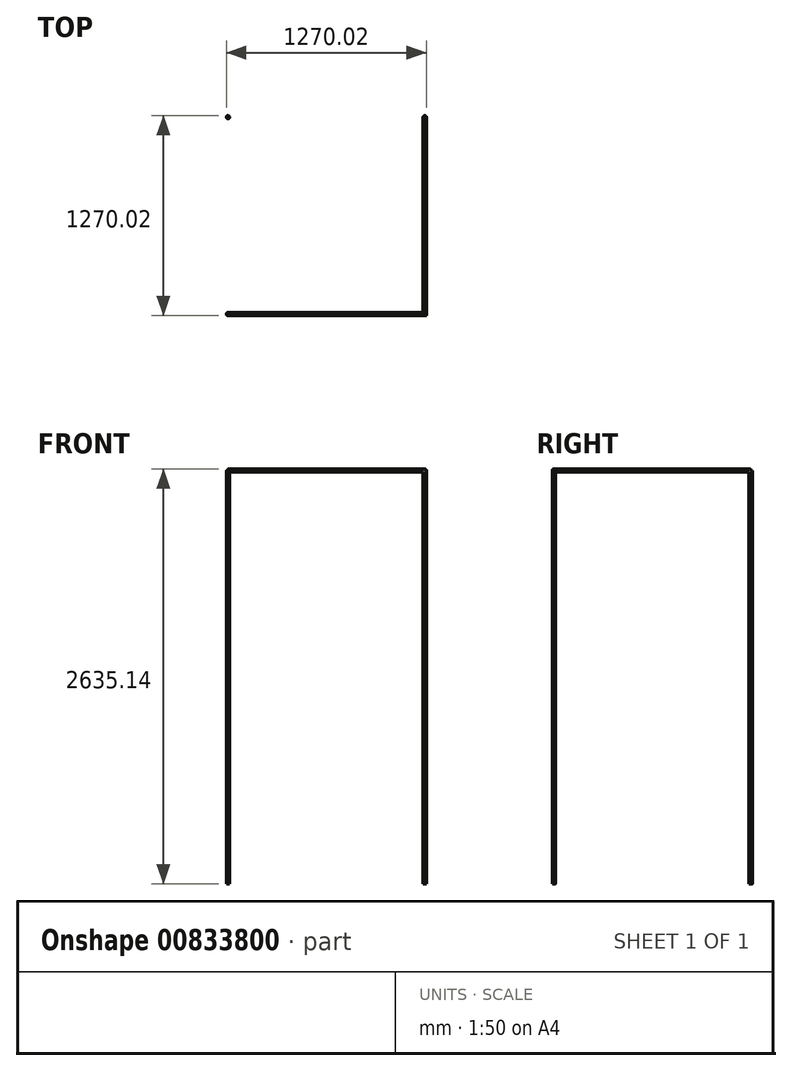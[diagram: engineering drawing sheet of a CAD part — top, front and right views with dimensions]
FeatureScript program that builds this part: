
annotation { "Feature Type Name" : "Feature", "Feature Type Description" : "" }
export const myFeature = defineFeature(function(context is Context, id is Id, definition is map)
    precondition{}
    {
        {
            var Q0;
            Q0=qCreatedBy(makeId("Top.planeOp"),FACE);
            var sketch = newSketch(context, id + "F0", { "sketchPlane" : qUnion([Q0])});
            skLineSegment(sketch, "E0", {"start": v(0, 0) * mm, "end": v(0, 1250) * mm});
            skLineSegment(sketch, "E1", {"start": v(0, 1250) * mm, "end": v(-1250, 1250) * mm});
            skLineSegment(sketch, "E2", {"start": v(-1250, 1250) * mm, "end": v(-1250, 0) * mm});
            skLineSegment(sketch, "E3", {"start": v(-1250, 0) * mm, "end": v(0, 0) * mm});
            skCircle(sketch, "E4", {"center": v(-1250, 1250) * mm, "radius": 10 * mm});
            skCircle(sketch, "E5", {"center": v(-1250, 0) * mm, "radius": 10 * mm});
            skCircle(sketch, "E6", {"center": v(0, 1250) * mm, "radius": 10 * mm});
            skCircle(sketch, "E7", {"center": v(0, 0) * mm, "radius": 10 * mm});
            skSolve(sketch);
        }
        {
            var Q0;
            {var subQ0=sQuery(id+"F0.wireOp",EDGE,"E1");var subQ1=sQuery(id+"F0.wireOp",EDGE,"E0");var subQ2=makeQuery(id+"F0.imprint","INTERSECT",VERTEX,{"derivedFrom":[subQ1,subQ0]});Q0=makeQuery(id+"F0.imprint","IMPRINT",FACE,{"disambiguationData":[TD([[makeQuery(id+"F0.imprint","IMPRINT",EDGE,{"disambiguationData":[TD([[subQ2,1.0]])],"derivedFrom":subQ1}),-1.0]])]});}
            var Q1;
            {var subQ0=sQuery(id+"F0.wireOp",EDGE,"E1");var subQ1=sQuery(id+"F0.wireOp",EDGE,"E0");var subQ2=makeQuery(id+"F0.imprint","INTERSECT",VERTEX,{"derivedFrom":[subQ1,subQ0]});Q1=makeQuery(id+"F0.imprint","IMPRINT",FACE,{"disambiguationData":[TD([[makeQuery(id+"F0.imprint","IMPRINT",EDGE,{"disambiguationData":[TD([[subQ2,1.0]])],"derivedFrom":subQ1}),1.0]])]});}
            var Q2;
            {var subQ0=sQuery(id+"F0.wireOp",EDGE,"E2");var subQ1=sQuery(id+"F0.wireOp",EDGE,"E1");var subQ2=makeQuery(id+"F0.imprint","INTERSECT",VERTEX,{"derivedFrom":[subQ1,subQ0]});Q2=makeQuery(id+"F0.imprint","IMPRINT",FACE,{"disambiguationData":[TD([[makeQuery(id+"F0.imprint","IMPRINT",EDGE,{"disambiguationData":[TD([[subQ2,1.0]])],"derivedFrom":subQ1}),-1.0]])]});}
            var Q3;
            {var subQ0=sQuery(id+"F0.wireOp",EDGE,"E2");var subQ1=sQuery(id+"F0.wireOp",EDGE,"E1");var subQ2=makeQuery(id+"F0.imprint","INTERSECT",VERTEX,{"derivedFrom":[subQ1,subQ0]});Q3=makeQuery(id+"F0.imprint","IMPRINT",FACE,{"disambiguationData":[TD([[makeQuery(id+"F0.imprint","IMPRINT",EDGE,{"disambiguationData":[TD([[subQ2,1.0]])],"derivedFrom":subQ1}),1.0]])]});}
            var Q4;
            {var subQ0=sQuery(id+"F0.wireOp",EDGE,"E3");var subQ1=sQuery(id+"F0.wireOp",EDGE,"E2");var subQ2=makeQuery(id+"F0.imprint","INTERSECT",VERTEX,{"derivedFrom":[subQ1,subQ0]});Q4=makeQuery(id+"F0.imprint","IMPRINT",FACE,{"disambiguationData":[TD([[makeQuery(id+"F0.imprint","IMPRINT",EDGE,{"disambiguationData":[TD([[subQ2,1.0]])],"derivedFrom":subQ1}),-1.0]])]});}
            var Q5;
            {var subQ0=sQuery(id+"F0.wireOp",EDGE,"E3");var subQ1=sQuery(id+"F0.wireOp",EDGE,"E2");var subQ2=makeQuery(id+"F0.imprint","INTERSECT",VERTEX,{"derivedFrom":[subQ1,subQ0]});Q5=makeQuery(id+"F0.imprint","IMPRINT",FACE,{"disambiguationData":[TD([[makeQuery(id+"F0.imprint","IMPRINT",EDGE,{"disambiguationData":[TD([[subQ2,1.0]])],"derivedFrom":subQ1}),1.0]])]});}
            var Q6;
            {var subQ0=sQuery(id+"F0.wireOp",EDGE,"E3");var subQ1=sQuery(id+"F0.wireOp",EDGE,"E0");var subQ2=makeQuery(id+"F0.imprint","INTERSECT",VERTEX,{"derivedFrom":[subQ1,subQ0]});Q6=makeQuery(id+"F0.imprint","IMPRINT",FACE,{"disambiguationData":[TD([[makeQuery(id+"F0.imprint","IMPRINT",EDGE,{"disambiguationData":[TD([[subQ2,-1.0]])],"derivedFrom":subQ1}),-1.0]])]});}
            var Q7;
            {var subQ0=sQuery(id+"F0.wireOp",EDGE,"E3");var subQ1=sQuery(id+"F0.wireOp",EDGE,"E0");var subQ2=makeQuery(id+"F0.imprint","INTERSECT",VERTEX,{"derivedFrom":[subQ1,subQ0]});Q7=makeQuery(id+"F0.imprint","IMPRINT",FACE,{"disambiguationData":[TD([[makeQuery(id+"F0.imprint","IMPRINT",EDGE,{"disambiguationData":[TD([[subQ2,-1.0]])],"derivedFrom":subQ1}),1.0]])]});}
            extrude(context, id + "F1", {"entities" : qUnion([Q0, Q1, Q2, Q3, Q4, Q5, Q6, Q7]), "depth" : 2625 * mm, "offsetDistance" : 25 * mm});
        }
        {
            var Q0;
            Q0=makeQuery(id+"F1.opExtrude","CAP_FACE",FACE,{"disambiguationData":[OSD([sQuery(id+"F0.wireOp",EDGE,"E7")])],"isStart":false});
            var sketch = newSketch(context, id + "F2", { "sketchPlane" : qUnion([Q0])});
            skLineSegment(sketch, "E8", {"start": v(0, 0) * mm, "end": v(0, 1249.75) * mm});
            skLineSegment(sketch, "E9", {"start": v(0, 0) * mm, "end": v(-1249.64, 0) * mm});
            skSolve(sketch);
        }
        {
            var Q0;
            Q0=sQuery(id+"F2.wireOp",VERTEX,"E8.start");
            var Q1;
            Q1=sQuery(id+"F2.wireOp",EDGE,"E8");
            cPlane(context, id + "F3", {"entities" : qUnion([Q0, Q1]), "cplaneType" : CPlaneType.LINE_POINT, "offset" : 25 * mm, "width" : 150 * mm, "height" : 150 * mm});
        }
        {
            var Q0;
            Q0=qCreatedBy(id+"F3.planeOp",FACE);
            var sketch = newSketch(context, id + "F4", { "sketchPlane" : qUnion([Q0])});
            skCircle(sketch, "E10", {"center": v(0, 2625.12) * mm, "radius": 10.02 * mm});
            skSolve(sketch);
        }
        {
            var Q0;
            Q0=makeQuery(id+"F4.imprint","IMPRINT",FACE,{"disambiguationData":[TD([[makeQuery(id+"F4.imprint","IMPRINT",EDGE,{"derivedFrom":sQuery(id+"F4.wireOp",EDGE,"E10")}),1.0]])]});
            var Q1;
            Q1=sQuery(id+"F2.wireOp",EDGE,"E8");
            var Q2;
            Q2=sQuery(id+"F2.wireOp",EDGE,"E9");
            sweep(context, id + "F5", {"profiles" : qUnion([Q0]), "path" : qUnion([Q1, Q2])});
        }
    });
